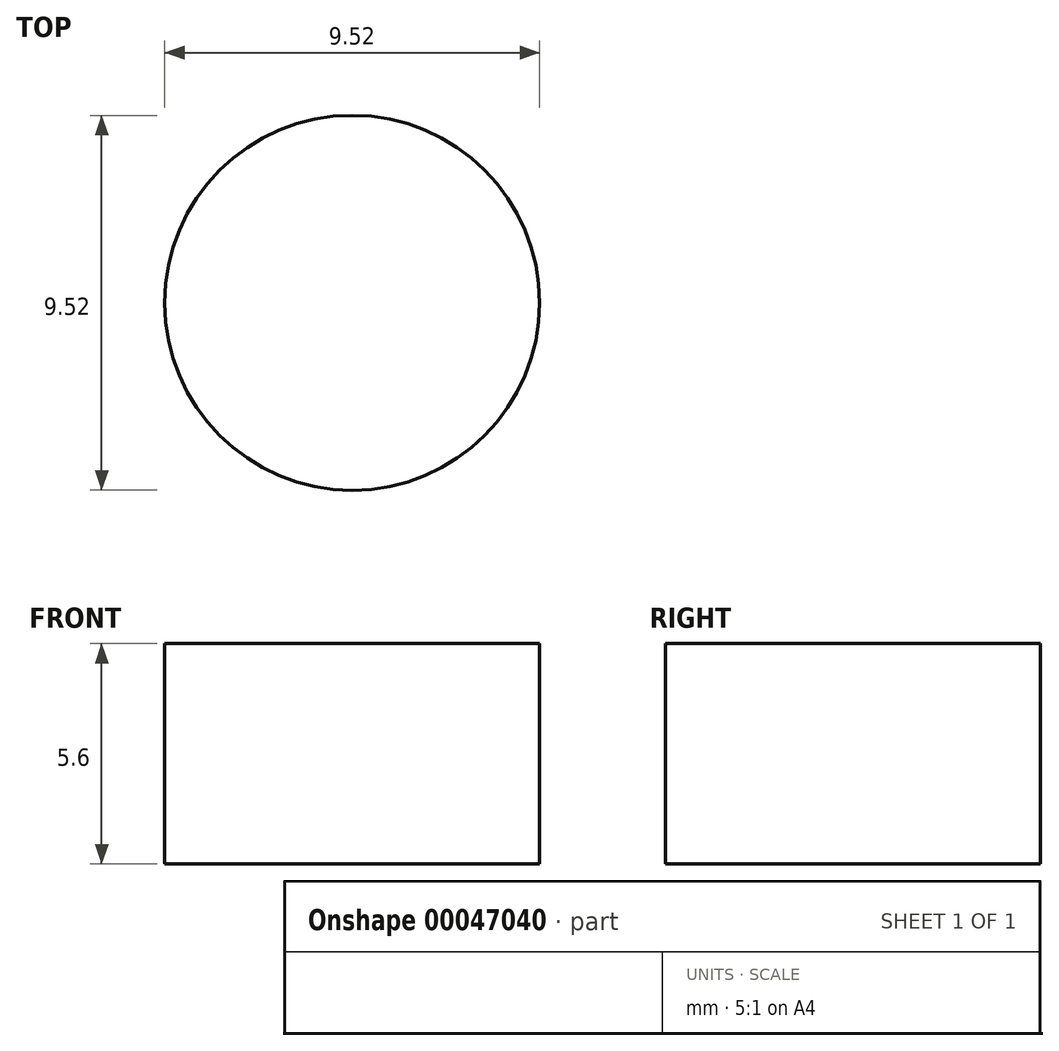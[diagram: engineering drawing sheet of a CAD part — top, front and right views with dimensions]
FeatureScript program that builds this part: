
annotation { "Feature Type Name" : "Feature", "Feature Type Description" : "" }
export const myFeature = defineFeature(function(context is Context, id is Id, definition is map)
    precondition{}
    {
        {
            var Q0;
            Q0=qCreatedBy(makeId("Top.planeOp"),FACE);
            var sketch = newSketch(context, id + "F0", { "sketchPlane" : qUnion([Q0])});
            skCircle(sketch, "E0", {"center": v(0, 0) * mm, "radius": 4.76 * mm});
            skSolve(sketch);
        }
        {
            var Q0;
            Q0 = qSketchRegion(id + "F0", true);
            extrude(context, id + "F1", {"entities" : qUnion([Q0]), "depth" : 5.6 * mm});
        }
    });
